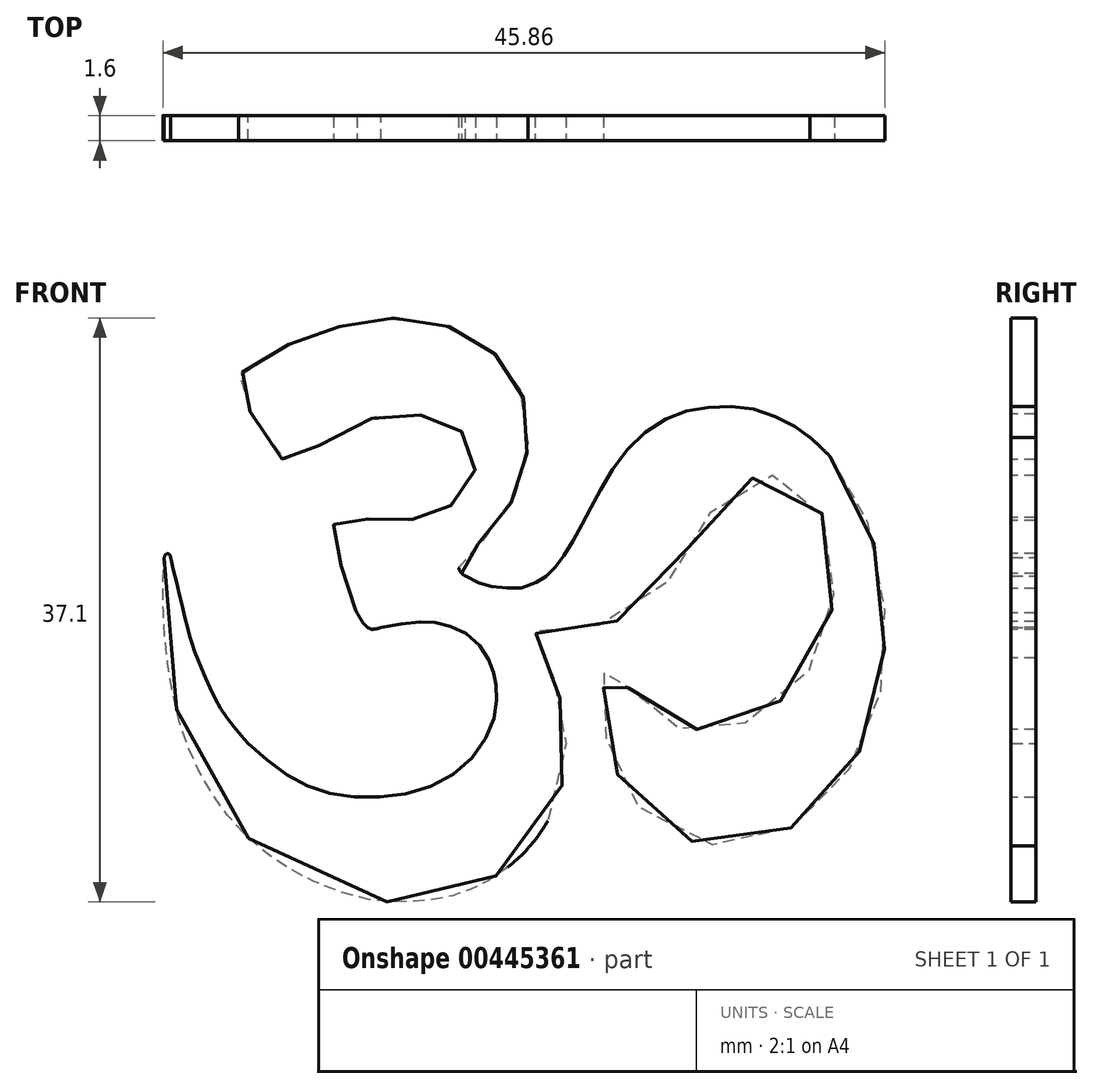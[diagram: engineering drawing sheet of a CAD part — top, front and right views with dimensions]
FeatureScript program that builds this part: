
annotation { "Feature Type Name" : "Feature", "Feature Type Description" : "" }
export const myFeature = defineFeature(function(context is Context, id is Id, definition is map)
    precondition{}
    {
        {
            var Q0;
            Q0=qCreatedBy(makeId("Front.planeOp"),FACE);
            var sketch = newSketch(context, id + "F0", { "sketchPlane" : qUnion([Q0])});
            skFitSpline(sketch, "E0", {"points": [v(-41.61, 16.15) * mm, v(-38.6, 13.82) * mm, v(-35.36, 12.81) * mm, v(-31.28, 13.02) * mm, v(-27.79, 14.82) * mm, v(-26.04, 17.58) * mm, v(-25.84, 19.5) * mm, v(-26, 20.6) * mm, v(-26.45, 21.7) * mm, v(-27.72, 23.1) * mm, v(-29.36, 23.74) * mm, v(-30.76, 23.88) * mm, v(-33.17, 23.5) * mm], "startDerivative": vector(28.04, -24.85) * mm, "endDerivative": vector(-30.86, -6.05) * mm});
            skFitSpline(sketch, "E1", {"points": [v(-33.17, 23.5) * mm, v(-33.66, 23.4) * mm, v(-34, 23.5) * mm, v(-34.68, 24.44) * mm, v(-35.1, 25.68) * mm, v(-35.68, 27.49) * mm], "startDerivative": vector(-3.6, -1.01) * mm, "endDerivative": vector(-2.25, 6.74) * mm});
            skFitSpline(sketch, "E2", {"points": [v(-34.68, 24.44) * mm, v(-34.96, 25.1) * mm, v(-35.3, 26.12) * mm, v(-35.6, 27.06) * mm, v(-35.9, 28.13) * mm, v(-36.05, 28.98) * mm, v(-36.16, 29.65) * mm, v(-36.15, 30.13) * mm, v(-35.86, 30.38) * mm, v(-35.6, 30.47) * mm, v(-34.8, 30.47) * mm, v(-33.8, 30.4) * mm, v(-32.88, 30.32) * mm, v(-32.06, 30.3) * mm, v(-31.16, 30.37) * mm, v(-30.34, 30.53) * mm, v(-29.63, 30.77) * mm, v(-28.93, 31.12) * mm, v(-28.34, 31.55) * mm, v(-27.72, 32.18) * mm, v(-27.3, 32.98) * mm, v(-27.16, 34) * mm, v(-27.26, 34.9) * mm, v(-27.64, 35.53) * mm, v(-28.16, 36.05) * mm, v(-28.89, 36.5) * mm, v(-29.68, 36.8) * mm, v(-30.73, 37.03) * mm, v(-31.95, 37.07) * mm, v(-32.92, 37) * mm, v(-34.03, 36.72) * mm, v(-35.28, 36.15) * mm, v(-36.86, 35.24) * mm, v(-38.1, 34.5) * mm, v(-38.66, 34.26) * mm, v(-39.11, 34.19) * mm, v(-39.49, 34.25) * mm, v(-40.3, 35.36) * mm, v(-41.17, 36.72) * mm, v(-41.87, 37.92) * mm, v(-42.16, 38.73) * mm, v(-42.18, 39.37) * mm, v(-41.81, 39.92) * mm, v(-40.74, 40.66) * mm, v(-39.44, 41.31) * mm, v(-38.19, 41.85) * mm, v(-36.96, 42.29) * mm, v(-35.68, 42.66) * mm, v(-34.35, 43) * mm, v(-33.04, 43.14) * mm, v(-31.64, 43.17) * mm, v(-30.27, 42.98) * mm, v(-28.8, 42.61) * mm, v(-27.45, 41.98) * mm, v(-26.43, 41.32) * mm, v(-25.63, 40.56) * mm, v(-24.97, 39.71) * mm, v(-24.25, 38.42) * mm, v(-23.9, 37.08) * mm, v(-23.82, 35.7) * mm, v(-23.94, 34.28) * mm, v(-24.2, 33.08) * mm, v(-24.68, 31.9) * mm, v(-25.27, 30.8) * mm, v(-26.02, 29.8) * mm, v(-26.91, 28.9) * mm, v(-27.76, 28.1) * mm, v(-28.14, 27.71) * mm, v(-28.23, 27.35) * mm, v(-28.05, 26.95) * mm, v(-27.55, 26.65) * mm], "startDerivative": vector(-23.11, 50.88) * mm, "endDerivative": vector(50.77, -23.54) * mm});
            skLineSegment(sketch, "E3", {"start": v(-28.05, 26.95) * mm, "end": v(-27.83, 27.1) * mm});
            skLineSegment(sketch, "E4", {"start": v(-28.05, 26.95) * mm, "end": v(-28.18, 26.86) * mm});
            skFitSpline(sketch, "E5", {"points": [v(-28.05, 26.95) * mm, v(-27.35, 26.5) * mm, v(-26.69, 26.25) * mm, v(-26.19, 26.13) * mm, v(-25.41, 26.02) * mm, v(-24.71, 26.02) * mm, v(-24.05, 26.07) * mm, v(-23.31, 26.38) * mm, v(-22.9, 26.6) * mm, v(-22.56, 26.87) * mm, v(-22.18, 27.25) * mm, v(-21.71, 27.83) * mm, v(-21.25, 28.55) * mm, v(-20.73, 29.41) * mm, v(-20.2, 30.47) * mm, v(-19.61, 31.55) * mm, v(-18.9, 32.87) * mm, v(-17.73, 34.54) * mm, v(-16.37, 35.92) * mm, v(-14.67, 36.93) * mm, v(-13.23, 37.37) * mm, v(-11.6, 37.55) * mm, v(-9.86, 37.46) * mm, v(-8.32, 37) * mm, v(-6.82, 36.27) * mm, v(-5.91, 35.59) * mm, v(-4.93, 34.7) * mm, v(-4, 33.5) * mm], "startDerivative": vector(21.05, -15.5) * mm, "endDerivative": vector(20.53, -28.82) * mm});
            skLineSegment(sketch, "E6", {"start": v(-5.91, 35.59) * mm, "end": v(-5.46, 35.77) * mm});
            skLineSegment(sketch, "E7", {"start": v(-5.91, 35.59) * mm, "end": v(-6.07, 35.5) * mm});
            skFitSpline(sketch, "E8", {"points": [v(-5.91, 35.59) * mm, v(-5.21, 34.93) * mm, v(-4.45, 34.15) * mm, v(-3.64, 33.05) * mm, v(-2.9, 31.78) * mm, v(-2.39, 30.55) * mm, v(-1.85, 28.83) * mm, v(-1.5, 26.85) * mm, v(-1.24, 25.04) * mm, v(-1.16, 23.67) * mm, v(-1.2, 22.06) * mm, v(-1.33, 20.24) * mm, v(-1.66, 18.44) * mm, v(-2.14, 17.1) * mm, v(-2.84, 15.5) * mm, v(-3.79, 14) * mm, v(-4.73, 12.7) * mm, v(-6.12, 11.43) * mm, v(-7.22, 10.72) * mm, v(-8.83, 10.05) * mm, v(-10.2, 9.68) * mm, v(-11.9, 9.7) * mm, v(-13.4, 9.92) * mm, v(-15.03, 10.7) * mm, v(-16.51, 11.8) * mm, v(-17.43, 12.91) * mm, v(-18.09, 14.05) * mm, v(-18.64, 15.42) * mm, v(-18.9, 16.77) * mm, v(-19.02, 17.81) * mm, v(-19.05, 18.96) * mm, v(-19.02, 19.81) * mm, v(-18.98, 20.82) * mm, v(-18.81, 21.48) * mm, v(-18.44, 21.54) * mm, v(-18.27, 21.29) * mm, v(-18.04, 20.77) * mm, v(-17.59, 19.91) * mm, v(-17.1, 19.2) * mm, v(-16.43, 18.39) * mm, v(-15.65, 17.71) * mm, v(-14.4, 17.17) * mm, v(-13.4, 17.03) * mm, v(-12.32, 17.04) * mm, v(-11.23, 17.11) * mm, v(-10.16, 17.41) * mm, v(-9.2, 17.9) * mm, v(-7.75, 18.9) * mm, v(-6.44, 20.23) * mm, v(-5.28, 21.85) * mm, v(-4.74, 23.5) * mm, v(-4.5, 24.77) * mm, v(-4.39, 25.98) * mm, v(-4.39, 27.21) * mm, v(-4.56, 28.57) * mm, v(-5.01, 30.42) * mm, v(-5.75, 31.88) * mm, v(-6.47, 32.66) * mm, v(-7.29, 33.05) * mm, v(-8.38, 33.18) * mm, v(-9.53, 33) * mm, v(-10.86, 32.32) * mm, v(-11.76, 31.4) * mm, v(-12.8, 30.08) * mm, v(-13.48, 28.9) * mm, v(-14.2, 27.64) * mm, v(-15.24, 26.01) * mm, v(-16.18, 25) * mm, v(-17.65, 24.15) * mm, v(-19.45, 23.62) * mm, v(-22.1, 23.5) * mm, v(-22.82, 23.5) * mm, v(-23.15, 23.5) * mm, v(-23.38, 23.48) * mm, v(-23.37, 23.33) * mm, v(-23.25, 22.86) * mm, v(-23.07, 22.35) * mm, v(-22.84, 21.76) * mm, v(-22.58, 21.17) * mm, v(-22.26, 20.4) * mm, v(-21.93, 19.5) * mm, v(-21.71, 18.66) * mm, v(-21.56, 17.58) * mm, v(-21.44, 16.58) * mm, v(-21.42, 15.41) * mm, v(-21.53, 14.12) * mm, v(-22.03, 12.36) * mm, v(-22.76, 10.92) * mm, v(-23.83, 9.48) * mm, v(-25.75, 7.81) * mm, v(-27.62, 6.82) * mm, v(-29.24, 6.33) * mm, v(-31.22, 6.12) * mm, v(-33.45, 6.15) * mm, v(-37.04, 7.2) * mm, v(-40.34, 9.1) * mm, v(-42.83, 11.48) * mm, v(-44.7, 14.35) * mm, v(-45.9, 17.34) * mm, v(-46.73, 21.31) * mm, v(-47, 24.54) * mm, v(-46.94, 27.96) * mm, v(-46.77, 28.29) * mm, v(-46.5, 28.3) * mm], "startDerivative": vector(86.37, -80.14) * mm, "endDerivative": vector(67.98, -4.77) * mm});
            skLineSegment(sketch, "E9", {"start": v(-46.94, 27.96) * mm, "end": v(-47.2, 27.96) * mm});
            skFitSpline(sketch, "E10", {"points": [v(-46.52, 27.96) * mm, v(-46.48, 27.73) * mm, v(-46.38, 27.27) * mm, v(-46.19, 26.5) * mm, v(-46, 25.7) * mm, v(-45.75, 24.69) * mm, v(-45.4, 23.36) * mm, v(-45.11, 22.3) * mm, v(-44.65, 21.1) * mm, v(-43.93, 19.46) * mm, v(-42.84, 17.63) * mm, v(-41.61, 16.15) * mm], "startDerivative": vector(0.75, -5.07) * mm, "endDerivative": vector(10.49, -11.78) * mm});
            skFitSpline(sketch, "E11", {"points": [v(-26.3, 48.76) * mm, v(-25.77, 48) * mm, v(-25.06, 46.96) * mm, v(-24.1, 45.82) * mm, v(-22.77, 44.68) * mm, v(-20.79, 43.75) * mm, v(-19, 43.46) * mm, v(-17.24, 43.5) * mm, v(-15.89, 43.82) * mm, v(-14.3, 44.55) * mm, v(-12.77, 45.4) * mm, v(-10.96, 46.64) * mm, v(-10.1, 47.31) * mm, v(-9.45, 47.62) * mm, v(-8.87, 47.6) * mm, v(-8.3, 47.2) * mm, v(-7.7, 46.55) * mm, v(-6.92, 45.58) * mm, v(-6.15, 44.5) * mm, v(-5.78, 43.3) * mm, v(-5.84, 42.54) * mm, v(-6.7, 41.68) * mm, v(-8, 40.8) * mm, v(-9.36, 40.05) * mm, v(-10.95, 39.43) * mm, v(-12.5, 38.93) * mm, v(-14.19, 38.54) * mm, v(-16.23, 38.35) * mm, v(-18.6, 38.6) * mm, v(-20.69, 39.1) * mm, v(-22.5, 40) * mm, v(-24.02, 41.23) * mm, v(-25.28, 42.75) * mm, v(-26.1, 44.66) * mm, v(-26.64, 46.66) * mm, v(-26.96, 48.44) * mm, v(-27.1, 49.25) * mm, v(-26.85, 49.5) * mm, v(-26.53, 49.38) * mm], "startDerivative": vector(24.59, -34.02) * mm, "endDerivative": vector(24.8, -17.03) * mm});
            skFitSpline(sketch, "E12", {"points": [v(-26.96, 48.44) * mm, v(-27.02, 49.14) * mm, v(-26.96, 49.36) * mm, v(-26.8, 49.4) * mm, v(-26.6, 49.16) * mm], "startDerivative": vector(-0.24, 2.14) * mm, "endDerivative": vector(0.8, -1.26) * mm});
            skFitSpline(sketch, "E13", {"points": [v(-26.6, 49.16) * mm, v(-26.48, 48.99) * mm, v(-26.3, 48.76) * mm], "startDerivative": vector(0.24, -0.36) * mm, "endDerivative": vector(0.32, -0.44) * mm});
            skFitSpline(sketch, "E14", {"points": [v(-46.94, 27.96) * mm, v(-46.86, 28.12) * mm, v(-46.72, 28.2) * mm, v(-46.62, 28.16) * mm, v(-46.55, 28.06) * mm, v(-46.52, 27.96) * mm], "startDerivative": vector(0.3, 0.66) * mm, "endDerivative": vector(0.16, -0.54) * mm});
            skFitSpline(sketch, "E15", {"points": [v(-21.73, 49.52) * mm, v(-21.14, 50.16) * mm, v(-20.04, 51.24) * mm, v(-19.22, 51.92) * mm, v(-18.83, 52.1) * mm, v(-18.39, 52.08) * mm, v(-17.6, 51.67) * mm, v(-16.73, 51.07) * mm, v(-15.94, 50.37) * mm, v(-15.26, 49.65) * mm, v(-14.95, 49.17) * mm, v(-14.83, 48.53) * mm, v(-14.97, 48) * mm, v(-15.4, 47.4) * mm, v(-15.97, 46.78) * mm, v(-16.57, 46.17) * mm, v(-17.19, 45.6) * mm, v(-17.76, 45.26) * mm, v(-18.16, 45.12) * mm, v(-18.58, 45.12) * mm, v(-19.15, 45.3) * mm, v(-19.85, 45.83) * mm, v(-20.5, 46.36) * mm, v(-21.06, 46.84) * mm, v(-21.64, 47.4) * mm, v(-22.27, 48) * mm], "startDerivative": vector(12.36, 14.01) * mm, "endDerivative": vector(-15.04, 14.19) * mm});
            skLineSegment(sketch, "E16", {"start": v(-21.06, 46.84) * mm, "end": v(-20.87, 47.02) * mm});
            skLineSegment(sketch, "E17", {"start": v(-21.06, 46.84) * mm, "end": v(-21.28, 46.64) * mm});
            skFitSpline(sketch, "E18", {"points": [v(-21.73, 49.52) * mm, v(-22, 49.19) * mm, v(-22.25, 48.82) * mm, v(-22.4, 48.44) * mm, v(-22.35, 48.08) * mm, v(-22, 47.67) * mm, v(-21.43, 47.16) * mm, v(-21.06, 46.84) * mm], "startDerivative": vector(-2.07, -2.4) * mm, "endDerivative": vector(2.43, -2.05) * mm});
            skFitSpline(sketch, "E19", {"points": [v(-6.7, 41.68) * mm, v(-6.17, 42.19) * mm, v(-5.82, 42.9) * mm, v(-5.78, 43.62) * mm, v(-6.15, 44.5) * mm], "startDerivative": vector(2.38, 1.92) * mm, "endDerivative": vector(-1.74, 3.22) * mm});
            skSolve(sketch);
        }
        {
            var Q0;
            Q0=makeQuery(id+"F0.imprint","IMPRINT",FACE,{"disambiguationData":[TD([[makeQuery(id+"F0.imprint","IMPRINT",EDGE,{"derivedFrom":sQuery(id+"F0.wireOp",EDGE,"E0")}),-1.0]])]});
            extrude(context, id + "F1", {"entities" : qUnion([Q0]), "depth" : 1.6 * mm});
        }
    });
